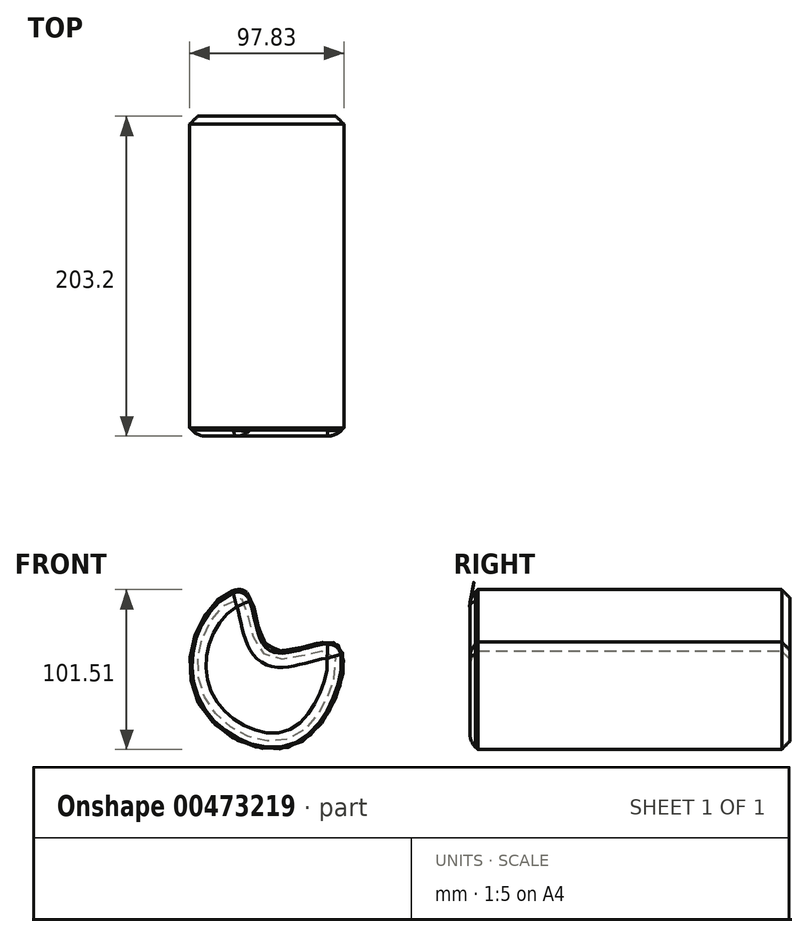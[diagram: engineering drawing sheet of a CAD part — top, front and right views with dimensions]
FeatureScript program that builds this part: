
annotation { "Feature Type Name" : "Feature", "Feature Type Description" : "" }
export const myFeature = defineFeature(function(context is Context, id is Id, definition is map)
    precondition{}
    {
        {
            var Q0;
            Q0=qCreatedBy(makeId("Front.planeOp"),FACE);
            var sketch = newSketch(context, id + "F0", { "sketchPlane" : qUnion([Q0])});
            skFitSpline(sketch, "E0", {"points": [v(-15.15, 52.85) * mm, v(-41.39, 39.54) * mm, v(-43.6, -21.43) * mm, v(20.7, -41.02) * mm, v(42.13, 19.96) * mm, v(0, 17) * mm, v(-15.15, 52.85) * mm]});
            skSolve(sketch);
        }
        {
            var Q0;
            Q0=makeQuery(id+"F0.imprint","IMPRINT",FACE,{"disambiguationData":[TD([[makeQuery(id+"F0.imprint","IMPRINT",EDGE,{"derivedFrom":sQuery(id+"F0.wireOp",EDGE,"E0")}),1.0]])]});
            extrude(context, id + "F1", {"entities" : qUnion([Q0]), "depth" : 25.4 * mm});
        }
        {
            var Q0;
            Q0=makeQuery(id+"F1.opExtrude","CAP_FACE",FACE,{"disambiguationData":[OSD([sQuery(id+"F0.wireOp",EDGE,"E0")])],"isStart":false});
            extrude(context, id + "F2", {"entities" : qUnion([Q0]), "operationType" : NewBodyOperationType.ADD, "depth" : 177.8 * mm});
        }
        {
            var Q0;
            Q0=makeQuery(id+"F2.opExtrude","CAP_FACE",FACE,{"disambiguationData":[OSD([sQuery(id+"F0.wireOp",EDGE,"E0")])],"isStart":false});
            var sketch = newSketch(context, id + "F3", { "sketchPlane" : qUnion([Q0])});
            skFitSpline(sketch, "E1.0", {"points": [v(49.11, -67.58) * mm, v(49.07, -67.59) * mm, v(49, -67.6) * mm, v(48.87, -67.63) * mm, v(48.77, -67.66) * mm, v(48.7, -67.68) * mm, v(48.64, -67.69) * mm, v(48.6, -67.7) * mm, v(48.57, -67.7) * mm, v(48.55, -67.71) * mm, v(48.53, -67.71) * mm, v(48.52, -67.72) * mm, v(48.5, -67.72) * mm, v(48.51, -67.72) * mm, v(48.51, -67.72) * mm, v(48.51, -67.72) * mm, v(48.51, -67.72) * mm, v(48.5, -67.72) * mm, v(48.5, -67.72) * mm, v(48.5, -67.72) * mm, v(48.5, -67.72) * mm, v(48.49, -67.72) * mm, v(48.47, -67.73) * mm, v(48.43, -67.74) * mm, v(48.34, -67.76) * mm, v(48.2, -67.8) * mm, v(48, -67.85) * mm, v(47.77, -67.9) * mm, v(47.41, -68) * mm, v(46.86, -68.15) * mm, v(45.79, -68.44) * mm, v(44.08, -68.9) * mm, v(41.47, -69.6) * mm, v(38.28, -70.42) * mm, v(34.49, -71.33) * mm, v(30, -72.29) * mm, v(24.73, -73.23) * mm, v(18.52, -74.08) * mm, v(11.16, -74.67) * mm, v(3.89, -74.76) * mm, v(-2.73, -74.39) * mm, v(-8.11, -73.82) * mm, v(-13.92, -72.9) * mm, v(-20.16, -71.53) * mm, v(-25.68, -69.93) * mm, v(-30.25, -68.33) * mm, v(-33.75, -66.96) * mm, v(-37.3, -65.42) * mm, v(-40, -64.12) * mm, v(-41.8, -63.19) * mm, v(-43, -62.55) * mm, v(-44.48, -61.74) * mm, v(-46.22, -60.73) * mm, v(-48.5, -59.36) * mm, v(-51.27, -57.58) * mm, v(-54.43, -55.36) * mm, v(-57.43, -53.08) * mm, v(-61.21, -49.98) * mm, v(-65.54, -46.02) * mm, v(-70.09, -41.25) * mm, v(-74.04, -36.55) * mm, v(-78.6, -30.48) * mm, v(-83.08, -23.35) * mm, v(-87.04, -15.7) * mm, v(-89.96, -8.96) * mm, v(-92.14, -3.07) * mm, v(-93.78, 2.06) * mm, v(-95.04, 6.5) * mm, v(-96.02, 10.33) * mm, v(-96.78, 13.57) * mm, v(-97.38, 16.24) * mm, v(-97.76, 18) * mm, v(-98, 19.1) * mm, v(-98.13, 19.67) * mm, v(-98.21, 20.04) * mm, v(-98.27, 20.28) * mm, v(-98.3, 20.48) * mm, v(-98.35, 20.63) * mm, v(-98.37, 20.72) * mm, v(-98.38, 20.76) * mm, v(-98.38, 20.78) * mm, v(-98.38, 20.79) * mm, v(-98.38, 20.8) * mm, v(-98.39, 20.8) * mm, v(-98.39, 20.8) * mm, v(-98.39, 20.8) * mm, v(-98.39, 20.8) * mm, v(-98.39, 20.8) * mm, v(-98.39, 20.8) * mm, v(-98.39, 20.8) * mm, v(-98.4, 20.82) * mm, v(-98.4, 20.83) * mm, v(-98.4, 20.86) * mm, v(-98.4, 20.88) * mm, v(-98.42, 20.92) * mm, v(-98.43, 20.97) * mm, v(-98.45, 21.04) * mm, v(-98.47, 21.14) * mm, v(-98.5, 21.25) * mm, v(-98.52, 21.32) * mm, v(-98.52, 21.36) * mm]});
            skSolve(sketch);
        }
        {
            var Q0;
            {var subQ0=sQuery(id+"F0.wireOp",EDGE,"E0");Q0=makeQuery(id+"F2.boolean.opBoolean","MERGE",FACE,{"derivedFrom":[makeQuery(id+"F1.opExtrude","SWEPT_FACE",FACE,{"disambiguationData":[OSD([subQ0])]}),makeQuery(id+"F2.opExtrude","SWEPT_FACE",FACE,{"disambiguationData":[OSD([subQ0])]})]});}
            chamfer(context, id + "F4", {"entities" : qUnion([Q0]), "width" : 5.08 * mm, "tangentPropagation" : true});
        }
        {
            var Q0;
            Q0=makeQuery(id+"F2.opExtrude","CAP_FACE",FACE,{"disambiguationData":[OSD([sQuery(id+"F0.wireOp",EDGE,"E0")])],"isStart":false});
            fillet(context, id + "F5", {"entities" : qUnion([Q0]), "radius" : 12.7 * mm, "tangentPropagation" : true, "allowEdgeOverflow" : false});
        }
    });
